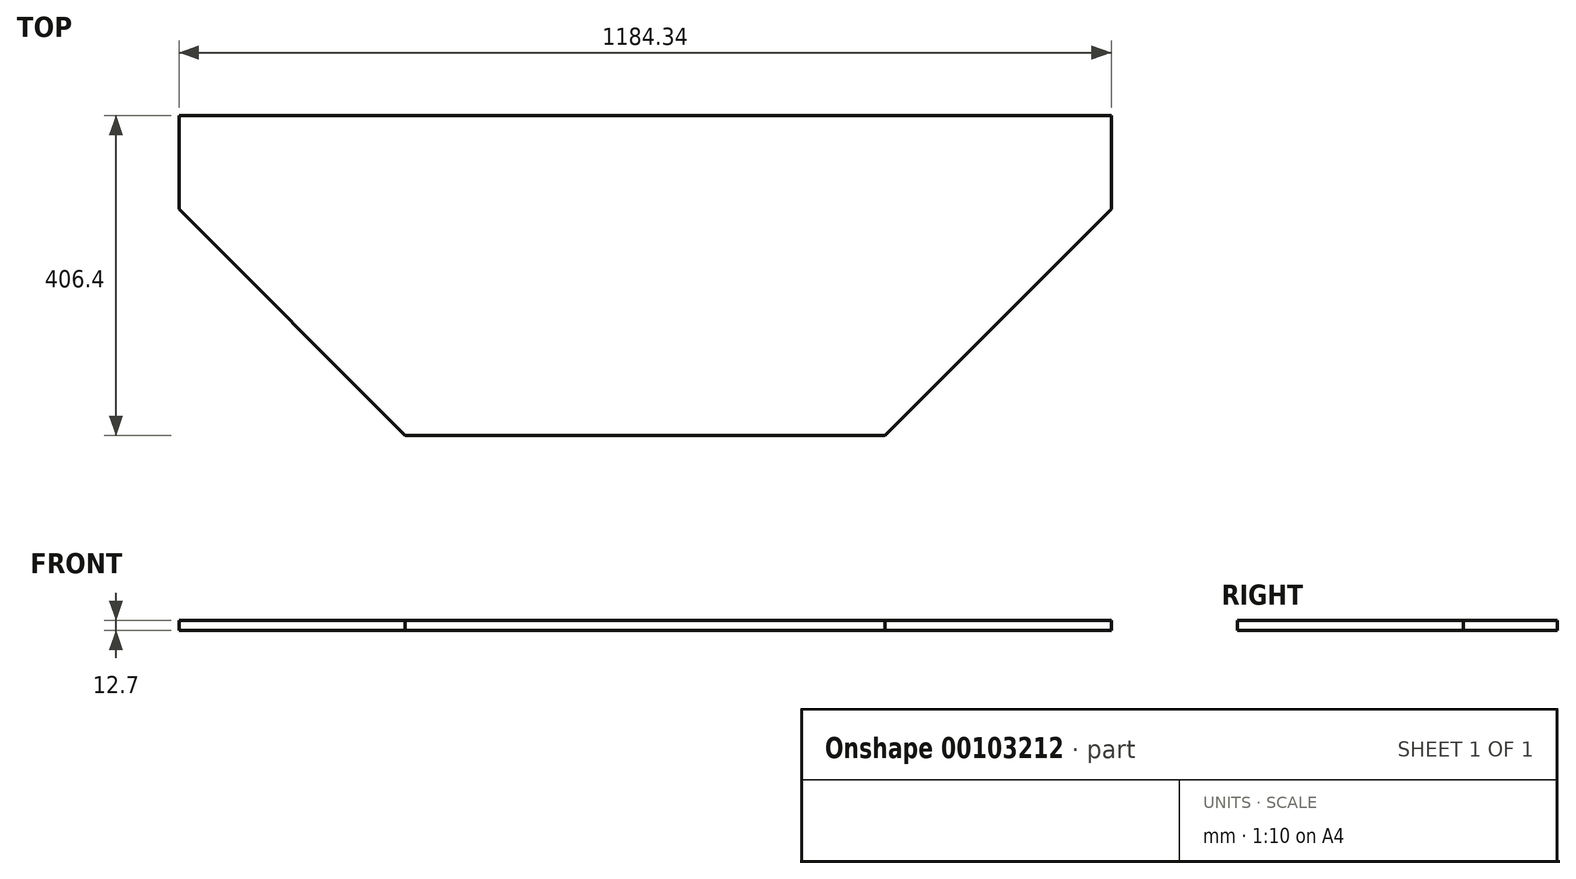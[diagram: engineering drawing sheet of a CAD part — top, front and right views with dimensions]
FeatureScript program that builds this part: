
annotation { "Feature Type Name" : "Feature", "Feature Type Description" : "" }
export const myFeature = defineFeature(function(context is Context, id is Id, definition is map)
    precondition{}
    {
        {
            var Q0;
            Q0=qCreatedBy(makeId("Top.planeOp"),FACE);
            var sketch = newSketch(context, id + "F0", { "sketchPlane" : qUnion([Q0])});
            skLineSegment(sketch, "E0", {"start": v(-304.8, -203.2) * mm, "end": v(-592.17, 84.17) * mm});
            skLineSegment(sketch, "E1", {"start": v(592.17, 84.17) * mm, "end": v(304.8, -203.2) * mm});
            skLineSegment(sketch, "E2", {"start": v(304.8, -203.2) * mm, "end": v(-304.8, -203.2) * mm});
            skLineSegment(sketch, "E3", {"start": v(0, -203.2) * mm, "end": v(0, 203.2) * mm, "construction": true});
            skLineSegment(sketch, "E4", {"start": v(-592.17, 84.17) * mm, "end": v(-592.17, 203.2) * mm});
            skLineSegment(sketch, "E5", {"start": v(-592.17, 203.2) * mm, "end": v(592.17, 203.2) * mm});
            skLineSegment(sketch, "E6", {"start": v(592.17, 203.2) * mm, "end": v(592.17, 84.17) * mm});
            skSolve(sketch);
        }
        {
            var Q0;
            Q0=makeQuery(id+"F0.imprint","IMPRINT",FACE,{"disambiguationData":[TD([[makeQuery(id+"F0.imprint","IMPRINT",EDGE,{"derivedFrom":sQuery(id+"F0.wireOp",EDGE,"E0")}),-1.0]])]});
            extrude(context, id + "F1", {"entities" : qUnion([Q0]), "endBound" : BoundingType.SYMMETRIC, "depth" : 12.7 * mm});
        }
    });
